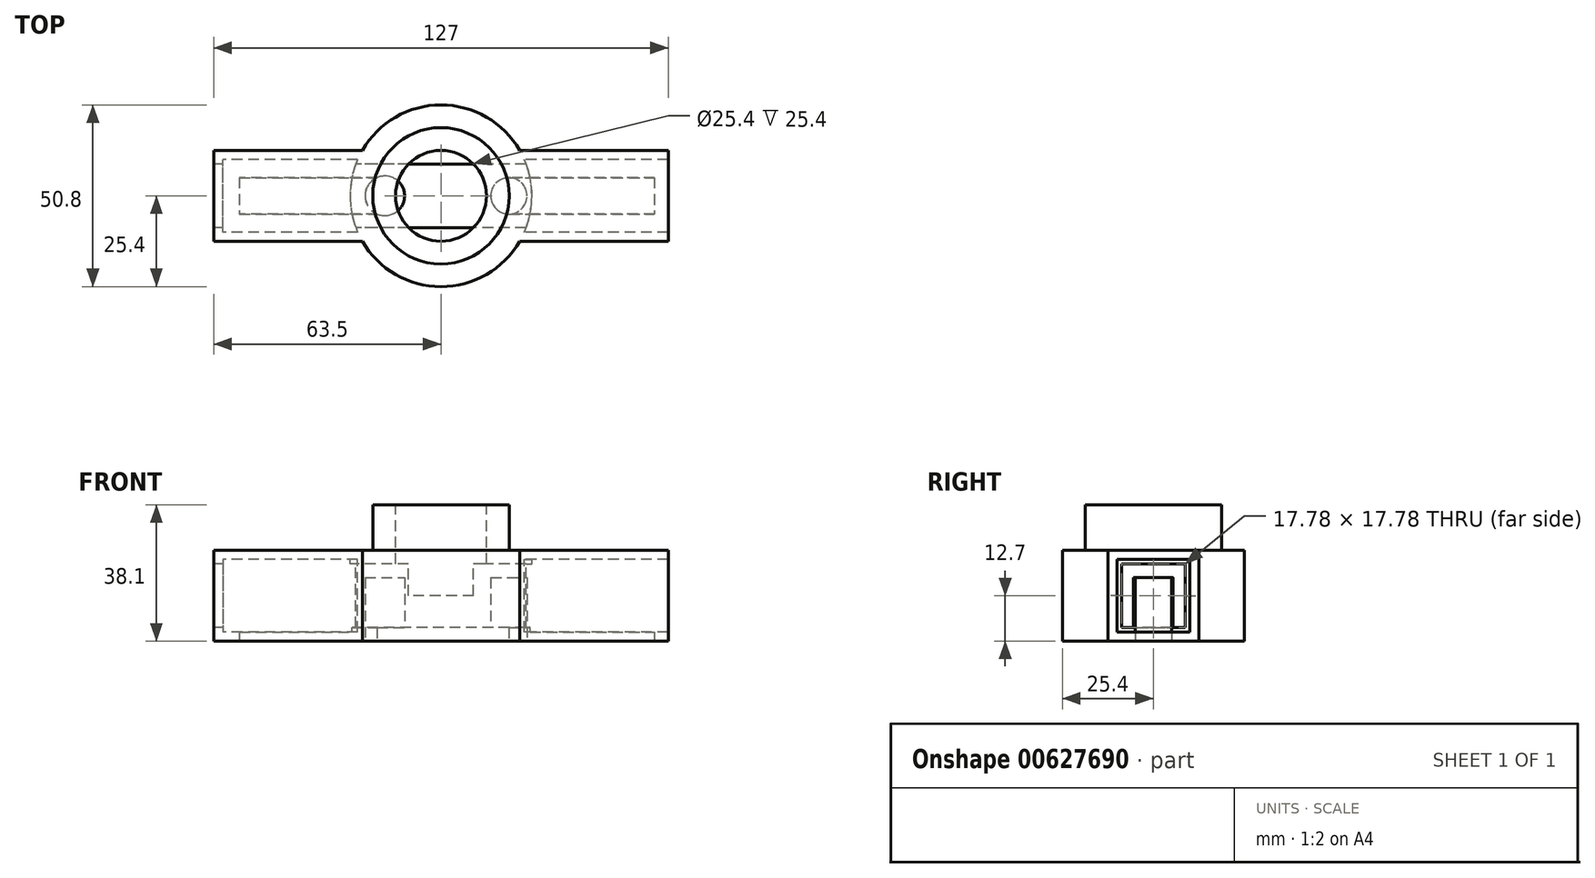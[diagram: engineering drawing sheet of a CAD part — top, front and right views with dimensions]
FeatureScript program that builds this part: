
annotation { "Feature Type Name" : "Feature", "Feature Type Description" : "" }
export const myFeature = defineFeature(function(context is Context, id is Id, definition is map)
    precondition{}
    {
        {
            var Q0;
            Q0=qCreatedBy(makeId("Top.planeOp"),FACE);
            var sketch = newSketch(context, id + "F0", { "sketchPlane" : qUnion([Q0])});
            skLineSegment(sketch, "E0.bottom", {"start": v(63.5, -12.7) * mm, "end": v(-63.5, -12.7) * mm});
            skLineSegment(sketch, "E0.top", {"start": v(63.5, 12.7) * mm, "end": v(-63.5, 12.7) * mm});
            skLineSegment(sketch, "E0.left", {"start": v(63.5, -12.7) * mm, "end": v(63.5, 12.7) * mm});
            skLineSegment(sketch, "E0.right", {"start": v(-63.5, -12.7) * mm, "end": v(-63.5, 12.7) * mm});
            skPoint(sketch, "E0.middle", {"position": v(0, 0) * mm});
            skSolve(sketch);
        }
        {
            var Q0;
            Q0 = qSketchRegion(id + "F0", true);
            extrude(context, id + "F1", {"entities" : qUnion([Q0]), "depth" : 25.4 * mm, "offsetDistance" : 25.4 * mm});
        }
        {
            var Q0;
            Q0=makeQuery(id+"F1.opExtrude","SWEPT_FACE",FACE,{"disambiguationData":[OSD([sQuery(id+"F0.wireOp",EDGE,"E0.left")])]});
            shell(context, id + "F2", {"entities" : qUnion([Q0]), "thickness" : 2.54 * mm});
        }
        {
            var Q0;
            Q0=makeQuery(id+"F1.opExtrude","CAP_FACE",FACE,{"disambiguationData":[OSD([sQuery(id+"F0.wireOp",EDGE,"E0.bottom"),sQuery(id+"F0.wireOp",EDGE,"E0.top"),sQuery(id+"F0.wireOp",EDGE,"E0.left"),sQuery(id+"F0.wireOp",EDGE,"E0.right")])],"isStart":false});
            var sketch = newSketch(context, id + "F3", { "sketchPlane" : qUnion([Q0])});
            skCircle(sketch, "E1", {"center": v(0, 0) * mm, "radius": 25.4 * mm});
            skSolve(sketch);
        }
        {
            var Q0;
            Q0 = qSketchRegion(id + "F3", true);
            extrude(context, id + "F4", {"entities" : qUnion([Q0]), "operationType" : NewBodyOperationType.ADD, "oppositeDirection" : true, "depth" : 25.4 * mm, "offsetDistance" : 25.4 * mm});
        }
        {
            var Q0;
            Q0=makeQuery(id+"F4.boolean.opBoolean","MERGE",FACE,{"derivedFrom":[makeQuery(id+"F1.opExtrude","CAP_FACE",FACE,{"disambiguationData":[OSD([sQuery(id+"F0.wireOp",EDGE,"E0.bottom"),sQuery(id+"F0.wireOp",EDGE,"E0.top"),sQuery(id+"F0.wireOp",EDGE,"E0.left"),sQuery(id+"F0.wireOp",EDGE,"E0.right")])],"isStart":false}),makeQuery(id+"F4.opExtrude","CAP_FACE",FACE,{"disambiguationData":[OSD([sQuery(id+"F3.wireOp",EDGE,"E1")])],"isStart":true})]});
            var sketch = newSketch(context, id + "F5", { "sketchPlane" : qUnion([Q0])});
            skCircle(sketch, "E2", {"center": v(0, 0) * mm, "radius": 19.05 * mm});
            skSolve(sketch);
        }
        {
            var Q0;
            Q0 = qSketchRegion(id + "F5", true);
            extrude(context, id + "F6", {"entities" : qUnion([Q0]), "operationType" : NewBodyOperationType.ADD, "depth" : 12.7 * mm, "offsetDistance" : 25.4 * mm});
        }
        {
            var Q0;
            Q0=makeQuery(id+"F6.opExtrude","CAP_FACE",FACE,{"disambiguationData":[OSD([sQuery(id+"F5.wireOp",EDGE,"E2")])],"isStart":false});
            var sketch = newSketch(context, id + "F7", { "sketchPlane" : qUnion([Q0])});
            skCircle(sketch, "E3", {"center": v(0, 0) * mm, "radius": 12.7 * mm});
            skSolve(sketch);
        }
        {
            var Q0;
            Q0 = qSketchRegion(id + "F7", true);
            extrude(context, id + "F8", {"entities" : qUnion([Q0]), "operationType" : NewBodyOperationType.REMOVE, "oppositeDirection" : true, "depth" : 25.4 * mm, "offsetDistance" : 25.4 * mm});
        }
        {
            var Q0;
            Q0=makeQuery(id+"F1.opExtrude","SWEPT_FACE",FACE,{"disambiguationData":[OSD([sQuery(id+"F0.wireOp",EDGE,"E0.right")])]});
            var sketch = newSketch(context, id + "F9", { "sketchPlane" : qUnion([Q0])});
            skLineSegment(sketch, "E4.bottom", {"start": v(8.89, 21.6) * mm, "end": v(-8.89, 21.6) * mm});
            skLineSegment(sketch, "E4.top", {"start": v(8.89, 3.81) * mm, "end": v(-8.89, 3.81) * mm});
            skLineSegment(sketch, "E4.left", {"start": v(8.89, 21.6) * mm, "end": v(8.89, 3.81) * mm});
            skLineSegment(sketch, "E4.right", {"start": v(-8.89, 21.6) * mm, "end": v(-8.89, 3.81) * mm});
            skPoint(sketch, "E4.middle", {"position": v(0, 12.7) * mm});
            skPoint(sketch, "E4.middle.positionSnap0", {"position": v(12.7, 12.7) * mm});
            skPoint(sketch, "E4.middle.positionSnap1", {"position": v(0, 25.4) * mm});
            skPoint(sketch, "E4.centerSnap0", {"position": v(12.7, 12.7) * mm});
            skPoint(sketch, "E4.centerSnap1", {"position": v(0, 25.4) * mm});
            skSolve(sketch);
        }
        {
            var Q0;
            Q0 = qSketchRegion(id + "F9", true);
            extrude(context, id + "F10", {"entities" : qUnion([Q0]), "operationType" : NewBodyOperationType.REMOVE, "oppositeDirection" : true, "depth" : 150.62 * mm, "offsetDistance" : 25.4 * mm});
        }
        {
            var Q0;
            Q0=makeQuery(id+"F4.boolean.opBoolean","MERGE",FACE,{"derivedFrom":[makeQuery(id+"F1.opExtrude","CAP_FACE",FACE,{"disambiguationData":[OSD([sQuery(id+"F0.wireOp",EDGE,"E0.bottom"),sQuery(id+"F0.wireOp",EDGE,"E0.top"),sQuery(id+"F0.wireOp",EDGE,"E0.left"),sQuery(id+"F0.wireOp",EDGE,"E0.right")])],"isStart":true}),makeQuery(id+"F4.opExtrude","CAP_FACE",FACE,{"disambiguationData":[OSD([sQuery(id+"F3.wireOp",EDGE,"E1")])],"isStart":false})]});
            var sketch = newSketch(context, id + "F11", { "sketchPlane" : qUnion([Q0])});
            skLineSegment(sketch, "E5.bottom", {"start": v(-15.69, -5.08) * mm, "end": v(-56.33, -5.08) * mm});
            skLineSegment(sketch, "E5.top", {"start": v(-15.69, 5.08) * mm, "end": v(-56.33, 5.08) * mm});
            skLineSegment(sketch, "E5.left", {"start": v(-15.69, -5.08) * mm, "end": v(-15.69, 5.08) * mm});
            skLineSegment(sketch, "E5.right", {"start": v(-56.33, -5.08) * mm, "end": v(-56.33, 5.08) * mm});
            skPoint(sketch, "E5.middle", {"position": v(-36, 0) * mm});
            skLineSegment(sketch, "E6.bottom", {"start": v(59.62, -5.08) * mm, "end": v(18.98, -5.08) * mm});
            skLineSegment(sketch, "E6.top", {"start": v(59.62, 5.08) * mm, "end": v(18.98, 5.08) * mm});
            skLineSegment(sketch, "E6.left", {"start": v(59.62, -5.08) * mm, "end": v(59.62, 5.08) * mm});
            skLineSegment(sketch, "E6.right", {"start": v(18.98, -5.08) * mm, "end": v(18.98, 5.08) * mm});
            skPoint(sketch, "E6.middle", {"position": v(39.3, 0) * mm});
            skSolve(sketch);
        }
        {
            var Q0;
            Q0 = qSketchRegion(id + "F11", true);
            extrude(context, id + "F12", {"entities" : qUnion([Q0]), "operationType" : NewBodyOperationType.REMOVE, "oppositeDirection" : true, "depth" : 12.7 * mm, "offsetDistance" : 25.4 * mm});
        }
        {
            var Q0;
            Q0=makeQuery(id+"F4.boolean.opBoolean","MERGE",FACE,{"derivedFrom":[makeQuery(id+"F1.opExtrude","CAP_FACE",FACE,{"disambiguationData":[OSD([sQuery(id+"F0.wireOp",EDGE,"E0.bottom"),sQuery(id+"F0.wireOp",EDGE,"E0.top"),sQuery(id+"F0.wireOp",EDGE,"E0.left"),sQuery(id+"F0.wireOp",EDGE,"E0.right")])],"isStart":true}),makeQuery(id+"F4.opExtrude","CAP_FACE",FACE,{"disambiguationData":[OSD([sQuery(id+"F3.wireOp",EDGE,"E1")])],"isStart":false})]});
            var sketch = newSketch(context, id + "F13", { "sketchPlane" : qUnion([Q0])});
            skCircle(sketch, "E7", {"center": v(-15.69, 0) * mm, "radius": 5.53 * mm});
            skCircle(sketch, "E8", {"center": v(18.98, 0) * mm, "radius": 5.08 * mm});
            skSolve(sketch);
        }
        {
            var Q0;
            Q0 = qSketchRegion(id + "F13", true);
            extrude(context, id + "F14", {"entities" : qUnion([Q0]), "operationType" : NewBodyOperationType.ADD, "oppositeDirection" : true, "depth" : 17.78 * mm, "offsetDistance" : 25.4 * mm});
        }
    });
